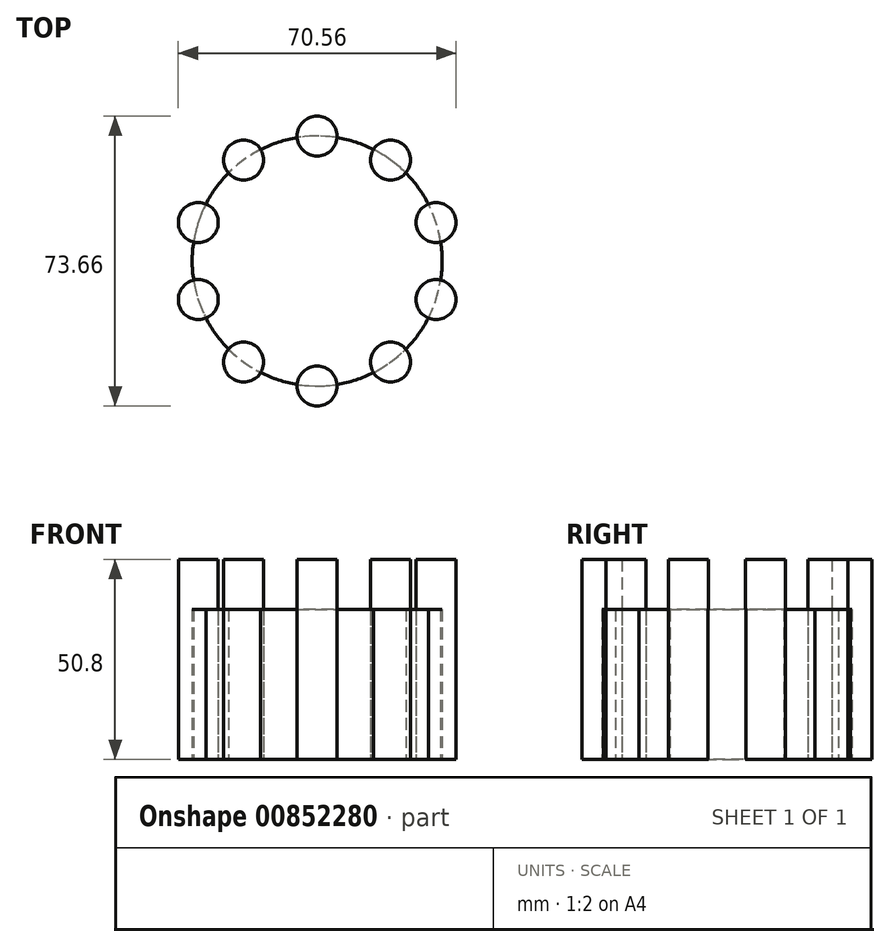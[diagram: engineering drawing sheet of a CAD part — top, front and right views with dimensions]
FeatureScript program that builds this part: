
annotation { "Feature Type Name" : "Feature", "Feature Type Description" : "" }
export const myFeature = defineFeature(function(context is Context, id is Id, definition is map)
    precondition{}
    {
        {
            var Q0;
            Q0=qCreatedBy(makeId("Top.planeOp"),FACE);
            var sketch = newSketch(context, id + "F0", { "sketchPlane" : qUnion([Q0])});
            skCircle(sketch, "E0", {"center": v(0, 0) * mm, "radius": 31.75 * mm});
            skSolve(sketch);
        }
        {
            var Q0;
            Q0=qSketchRegion(id+"F0",true);
            extrude(context, id + "F1", {"entities" : qUnion([Q0]), "depth" : 38.1 * mm});
        }
        {
            var Q0;
            Q0=qCreatedBy(makeId("Top.planeOp"),FACE);
            var sketch = newSketch(context, id + "F2", { "sketchPlane" : qUnion([Q0])});
            skCircle(sketch, "E1", {"center": v(0, 31.75) * mm, "radius": 5.08 * mm});
            skCircle(sketch, "E2.1.0", {"center": v(-18.66, 25.69) * mm, "radius": 5.08 * mm});
            skCircle(sketch, "E2.2.0", {"center": v(-30.2, 9.81) * mm, "radius": 5.08 * mm});
            skCircle(sketch, "E2.3.0", {"center": v(-30.2, -9.81) * mm, "radius": 5.08 * mm});
            skCircle(sketch, "E2.4.0", {"center": v(-18.66, -25.69) * mm, "radius": 5.08 * mm});
            skCircle(sketch, "E2.5.0", {"center": v(0, -31.75) * mm, "radius": 5.08 * mm});
            skCircle(sketch, "E2.6.0", {"center": v(18.66, -25.69) * mm, "radius": 5.08 * mm});
            skCircle(sketch, "E2.7.0", {"center": v(30.2, -9.81) * mm, "radius": 5.08 * mm});
            skCircle(sketch, "E2.8.0", {"center": v(30.2, 9.81) * mm, "radius": 5.08 * mm});
            skCircle(sketch, "E2.9.0", {"center": v(18.66, 25.69) * mm, "radius": 5.08 * mm});
            skPoint(sketch, "E2.center", {"position": v(0, 0) * mm});
            skSolve(sketch);
        }
        {
            var Q0;
            Q0=qSketchRegion(id+"F2",true);
            extrude(context, id + "F3", {"entities" : qUnion([Q0]), "depth" : 50.8 * mm});
        }
        {
            var Q0;
            Q0=makeQuery(id+"F1.opExtrude","SWEPT_BODY",BODY,{"disambiguationData":[OSD([sQuery(id+"F0.wireOp",EDGE,"E0")])]});
            var Q1;
            Q1=makeQuery(id+"F3.opExtrude","SWEPT_BODY",BODY,{"disambiguationData":[OSD([sQuery(id+"F2.wireOp",EDGE,"E2.3.0")])]});
            booleanBodies(context, id + "F4", {"operationType" : BooleanOperationType.INTERSECTION, "tools" : qUnion([Q0, Q1]), "keepTools" : true});
        }
        {
            var Q0;
            Q0=makeQuery(id+"F1.opExtrude","SWEPT_BODY",BODY,{"disambiguationData":[OSD([sQuery(id+"F0.wireOp",EDGE,"E0")])]});
            var Q1;
            Q1=makeQuery(id+"F3.opExtrude","SWEPT_BODY",BODY,{"disambiguationData":[OSD([sQuery(id+"F2.wireOp",EDGE,"E2.2.0")])]});
            booleanBodies(context, id + "F5", {"operationType" : BooleanOperationType.INTERSECTION, "tools" : qUnion([Q0, Q1]), "keepTools" : true});
        }
        {
            var Q0;
            Q0=makeQuery(id+"F1.opExtrude","SWEPT_BODY",BODY,{"disambiguationData":[OSD([sQuery(id+"F0.wireOp",EDGE,"E0")])]});
            var Q1;
            Q1=makeQuery(id+"F3.opExtrude","SWEPT_BODY",BODY,{"disambiguationData":[OSD([sQuery(id+"F2.wireOp",EDGE,"E2.1.0")])]});
            booleanBodies(context, id + "F6", {"operationType" : BooleanOperationType.INTERSECTION, "tools" : qUnion([Q0, Q1]), "keepTools" : true});
        }
        {
            var Q0;
            Q0=makeQuery(id+"F1.opExtrude","SWEPT_BODY",BODY,{"disambiguationData":[OSD([sQuery(id+"F0.wireOp",EDGE,"E0")])]});
            var Q1;
            Q1=makeQuery(id+"F3.opExtrude","SWEPT_BODY",BODY,{"disambiguationData":[OSD([sQuery(id+"F2.wireOp",EDGE,"E1")])]});
            booleanBodies(context, id + "F7", {"operationType" : BooleanOperationType.INTERSECTION, "tools" : qUnion([Q0, Q1]), "keepTools" : true});
        }
        {
            var Q0;
            Q0=makeQuery(id+"F1.opExtrude","SWEPT_BODY",BODY,{"disambiguationData":[OSD([sQuery(id+"F0.wireOp",EDGE,"E0")])]});
            var Q1;
            Q1=makeQuery(id+"F3.opExtrude","SWEPT_BODY",BODY,{"disambiguationData":[OSD([sQuery(id+"F2.wireOp",EDGE,"E2.9.0")])]});
            booleanBodies(context, id + "F8", {"operationType" : BooleanOperationType.INTERSECTION, "tools" : qUnion([Q0, Q1]), "keepTools" : true});
        }
        {
            var Q0;
            Q0=makeQuery(id+"F1.opExtrude","SWEPT_BODY",BODY,{"disambiguationData":[OSD([sQuery(id+"F0.wireOp",EDGE,"E0")])]});
            var Q1;
            Q1=makeQuery(id+"F3.opExtrude","SWEPT_BODY",BODY,{"disambiguationData":[OSD([sQuery(id+"F2.wireOp",EDGE,"E2.8.0")])]});
            booleanBodies(context, id + "F9", {"operationType" : BooleanOperationType.INTERSECTION, "tools" : qUnion([Q0, Q1]), "keepTools" : true});
        }
        {
            var Q0;
            Q0=makeQuery(id+"F1.opExtrude","SWEPT_BODY",BODY,{"disambiguationData":[OSD([sQuery(id+"F0.wireOp",EDGE,"E0")])]});
            var Q1;
            Q1=makeQuery(id+"F3.opExtrude","SWEPT_BODY",BODY,{"disambiguationData":[OSD([sQuery(id+"F2.wireOp",EDGE,"E2.7.0")])]});
            booleanBodies(context, id + "F10", {"operationType" : BooleanOperationType.INTERSECTION, "tools" : qUnion([Q0, Q1]), "keepTools" : true});
        }
        {
            var Q0;
            Q0=makeQuery(id+"F1.opExtrude","SWEPT_BODY",BODY,{"disambiguationData":[OSD([sQuery(id+"F0.wireOp",EDGE,"E0")])]});
            var Q1;
            Q1=makeQuery(id+"F3.opExtrude","SWEPT_BODY",BODY,{"disambiguationData":[OSD([sQuery(id+"F2.wireOp",EDGE,"E2.6.0")])]});
            booleanBodies(context, id + "F11", {"operationType" : BooleanOperationType.INTERSECTION, "tools" : qUnion([Q0, Q1]), "keepTools" : true});
        }
        {
            var Q0;
            Q0=makeQuery(id+"F1.opExtrude","SWEPT_BODY",BODY,{"disambiguationData":[OSD([sQuery(id+"F0.wireOp",EDGE,"E0")])]});
            var Q1;
            Q1=makeQuery(id+"F3.opExtrude","SWEPT_BODY",BODY,{"disambiguationData":[OSD([sQuery(id+"F2.wireOp",EDGE,"E2.5.0")])]});
            booleanBodies(context, id + "F12", {"operationType" : BooleanOperationType.INTERSECTION, "tools" : qUnion([Q0, Q1]), "keepTools" : true});
        }
        {
            var Q0;
            Q0=makeQuery(id+"F1.opExtrude","SWEPT_BODY",BODY,{"disambiguationData":[OSD([sQuery(id+"F0.wireOp",EDGE,"E0")])]});
            var Q1;
            Q1=makeQuery(id+"F3.opExtrude","SWEPT_BODY",BODY,{"disambiguationData":[OSD([sQuery(id+"F2.wireOp",EDGE,"E2.4.0")])]});
            booleanBodies(context, id + "F13", {"operationType" : BooleanOperationType.INTERSECTION, "tools" : qUnion([Q0, Q1]), "keepTools" : true});
        }
    });
